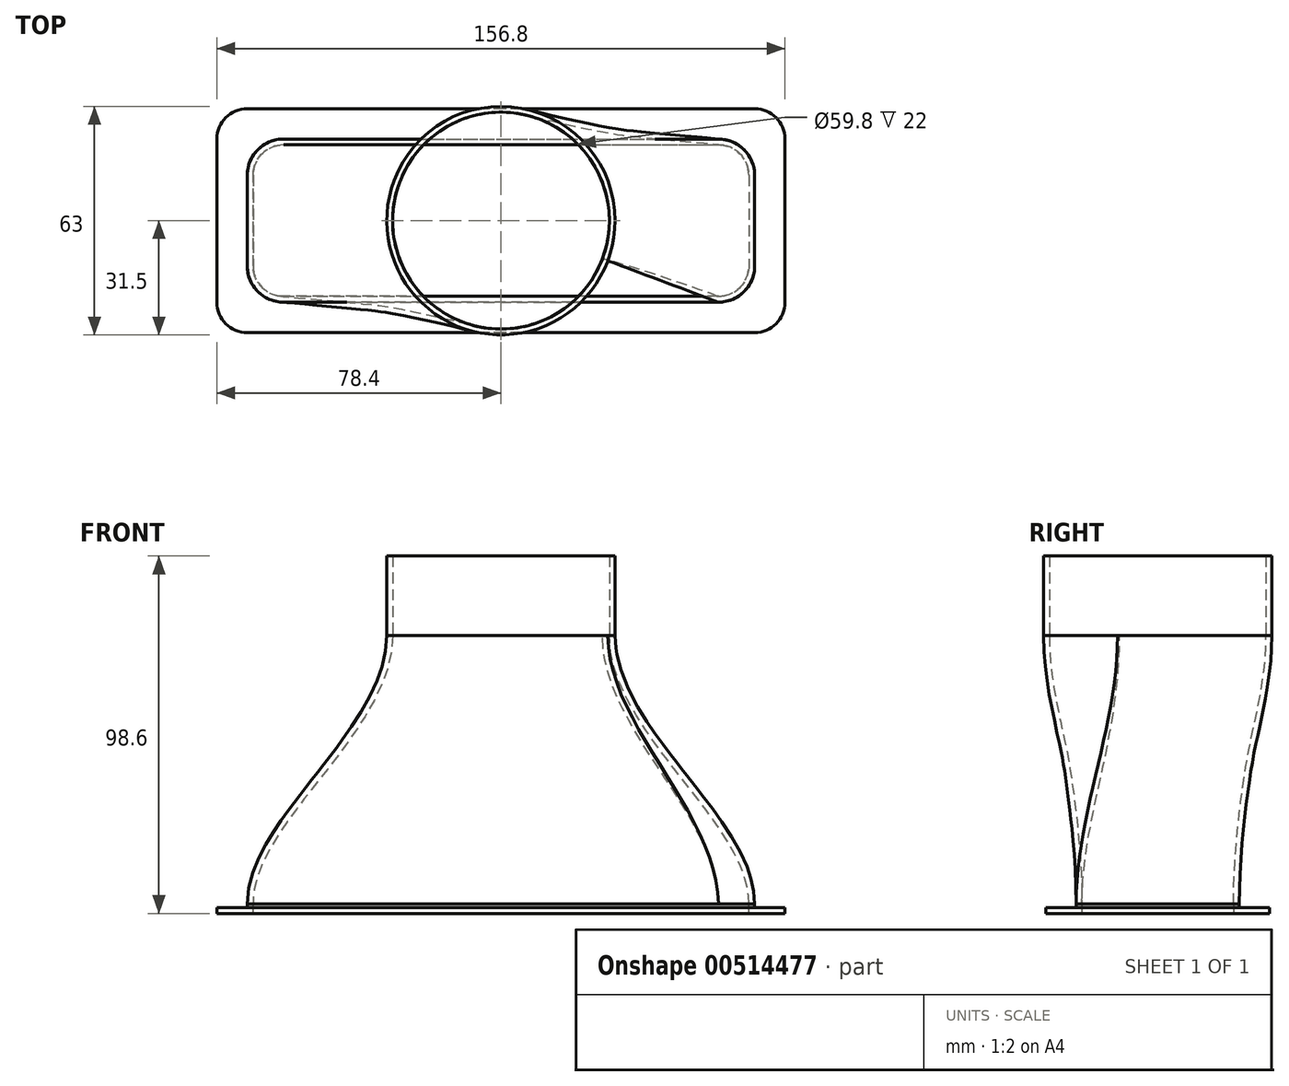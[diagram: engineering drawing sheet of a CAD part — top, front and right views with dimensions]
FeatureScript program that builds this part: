
annotation { "Feature Type Name" : "Feature", "Feature Type Description" : "" }
export const myFeature = defineFeature(function(context is Context, id is Id, definition is map)
    precondition{}
    {
        {
            var Q0;
            Q0=qCreatedBy(makeId("Top.planeOp"),FACE);
            var sketch = newSketch(context, id + "F0", { "sketchPlane" : qUnion([Q0])});
            skCircle(sketch, "E0", {"center": v(0, 0) * mm, "radius": 31.5 * mm});
            skSolve(sketch);
        }
        {
            var Q0;
            Q0 = qSketchRegion(id + "F0", true);
            extrude(context, id + "F1", {"entities" : qUnion([Q0]), "depth" : 100 * mm});
        }
        {
            var Q0;
            Q0=qCreatedBy(makeId("Top.planeOp"),FACE);
            var sketch = newSketch(context, id + "F2", { "sketchPlane" : qUnion([Q0])});
            skLineSegment(sketch, "E1.bottom", {"start": v(60, -22.5) * mm, "end": v(-60, -22.5) * mm});
            skLineSegment(sketch, "E1.top", {"start": v(60, 22.5) * mm, "end": v(-60, 22.5) * mm});
            skLineSegment(sketch, "E1.left", {"start": v(70, -12.5) * mm, "end": v(70, 12.5) * mm});
            skLineSegment(sketch, "E1.right", {"start": v(-70, -12.5) * mm, "end": v(-70, 12.5) * mm});
            skPoint(sketch, "E1.middle", {"position": v(0, 0) * mm});
            skPoint(sketch, "E2.visualSharp", {"position": v(-70, 22.5) * mm});
            skArc(sketch, "E2.filletArc", {"start": v(-60, 22.5) * mm, "mid": v(-67.07, 19.57) * mm, "end": v(-70, 12.5) * mm});
            skPoint(sketch, "E3.visualSharp", {"position": v(-70, -22.5) * mm});
            skArc(sketch, "E3.filletArc", {"start": v(-70, -12.5) * mm, "mid": v(-67.07, -19.57) * mm, "end": v(-60, -22.5) * mm});
            skPoint(sketch, "E4.visualSharp", {"position": v(70, 22.5) * mm});
            skArc(sketch, "E4.filletArc", {"start": v(70, 12.5) * mm, "mid": v(67.07, 19.57) * mm, "end": v(60, 22.5) * mm});
            skPoint(sketch, "E5.visualSharp", {"position": v(70, -22.5) * mm});
            skArc(sketch, "E5.filletArc", {"start": v(60, -22.5) * mm, "mid": v(67.07, -19.57) * mm, "end": v(70, -12.5) * mm});
            skSolve(sketch);
        }
        {
            var Q0;
            Q0=makeQuery(id+"F486plCCYYAXnXF_1.boolean.opBoolean","MERGE",FACE,{"derivedFrom":[makeQuery(id+"F1.opExtrude","CAP_FACE",FACE,{"disambiguationData":[OSD([sQuery(id+"F0.wireOp",EDGE,"E0")])],"isStart":true}),makeQuery(id+"F486plCCYYAXnXF_1.opExtrude","CAP_FACE",FACE,{"disambiguationData":[OSD([sQuery(id+"F2.wireOp",EDGE,"E1.bottom"),sQuery(id+"F2.wireOp",EDGE,"E1.top"),sQuery(id+"F2.wireOp",EDGE,"E1.left"),sQuery(id+"F2.wireOp",EDGE,"E1.right"),sQuery(id+"F2.wireOp",EDGE,"E2.filletArc"),sQuery(id+"F2.wireOp",EDGE,"E3.filletArc"),sQuery(id+"F2.wireOp",EDGE,"E4.filletArc"),sQuery(id+"F2.wireOp",EDGE,"E5.filletArc")])],"isStart":true})]});
            var sketch = newSketch(context, id + "F3", { "sketchPlane" : qUnion([Q0])});
            skCircle(sketch, "E6", {"center": v(0, 0) * mm, "radius": 31.5 * mm});
            skSolve(sketch);
        }
        {
            var Q0;
            Q0 = qSketchRegion(id + "F3", true);
            extrude(context, id + "F4", {"entities" : qUnion([Q0]), "operationType" : NewBodyOperationType.REMOVE, "oppositeDirection" : true, "depth" : 98 * mm});
        }
        {
            var Q0;
            Q0=makeQuery(id+"F2.imprint","IMPRINT",FACE,{"disambiguationData":[TD([[makeQuery(id+"F2.imprint","IMPRINT",EDGE,{"derivedFrom":sQuery(id+"F2.wireOp",EDGE,"E1.bottom")}),-1.0]])]});
            extrude(context, id + "F5", {"entities" : qUnion([Q0]), "depth" : 4 * mm});
        }
        {
            var Q0;
            Q0=makeQuery(id+"F4.boolean.opBoolean","COPY",FACE,{"derivedFrom":makeQuery(id+"F4.opExtrude","CAP_FACE",FACE,{"disambiguationData":[OSD([sQuery(id+"F3.wireOp",EDGE,"E6")])],"isStart":false})});
            extrude(context, id + "F6", {"entities" : qUnion([Q0]), "operationType" : NewBodyOperationType.ADD, "depth" : 20 * mm});
        }
        {
            var Q1;
            Q1=makeQuery(id+"F5.opExtrude","CAP_FACE",FACE,{"disambiguationData":[OSD([sQuery(id+"F2.wireOp",EDGE,"E1.bottom"),sQuery(id+"F2.wireOp",EDGE,"E1.top"),sQuery(id+"F2.wireOp",EDGE,"E1.left"),sQuery(id+"F2.wireOp",EDGE,"E1.right"),sQuery(id+"F2.wireOp",EDGE,"E2.filletArc"),sQuery(id+"F2.wireOp",EDGE,"E3.filletArc"),sQuery(id+"F2.wireOp",EDGE,"E4.filletArc"),sQuery(id+"F2.wireOp",EDGE,"E5.filletArc")])],"isStart":false});
            var Q2;
            Q2=makeQuery(id+"F6.opExtrude","CAP_FACE",FACE,{"disambiguationData":[OSD([sQuery(id+"F3.wireOp",EDGE,"E6")])],"isStart":false});
            loft(context, id + "F7", {"operationType" : NewBodyOperationType.ADD, "startCondition" : LoftEndDerivativeType.NORMAL_TO_PROFILE, "startMagnitude" : 1, "endCondition" : LoftEndDerivativeType.NORMAL_TO_PROFILE, "endMagnitude" : 1, "sheetProfilesArray" : [{ "sheetProfileEntities" : qUnion([Q1]) }, { "sheetProfileEntities" : qUnion([Q2]) }]});
        }
        {
            var Q0;
            Q0=makeQuery(id+"F5.opExtrude","CAP_FACE",FACE,{"disambiguationData":[OSD([sQuery(id+"F2.wireOp",EDGE,"E1.bottom"),sQuery(id+"F2.wireOp",EDGE,"E1.top"),sQuery(id+"F2.wireOp",EDGE,"E1.left"),sQuery(id+"F2.wireOp",EDGE,"E1.right"),sQuery(id+"F2.wireOp",EDGE,"E2.filletArc"),sQuery(id+"F2.wireOp",EDGE,"E3.filletArc"),sQuery(id+"F2.wireOp",EDGE,"E4.filletArc"),sQuery(id+"F2.wireOp",EDGE,"E5.filletArc")])],"isStart":true});
            var sketch = newSketch(context, id + "F8", { "sketchPlane" : qUnion([Q0])});
            skLineSegment(sketch, "E7.bottom", {"start": v(80, -32.5) * mm, "end": v(-80, -32.5) * mm});
            skLineSegment(sketch, "E7.top", {"start": v(80, 32.5) * mm, "end": v(-80, 32.5) * mm});
            skLineSegment(sketch, "E7.left", {"start": v(80, -32.5) * mm, "end": v(80, 32.5) * mm});
            skLineSegment(sketch, "E7.right", {"start": v(-80, -32.5) * mm, "end": v(-80, 32.5) * mm});
            skPoint(sketch, "E7.middle", {"position": v(0, 0) * mm});
            skSolve(sketch);
        }
        {
            var Q0;
            Q0 = qSketchRegion(id + "F8", true);
            extrude(context, id + "F9", {"entities" : qUnion([Q0]), "operationType" : NewBodyOperationType.ADD, "oppositeDirection" : true, "depth" : 3 * mm});
        }
        {
            var Q0;
            Q0=makeQuery(id+"F9.opExtrude","SWEPT_EDGE",EDGE,{"disambiguationData":[OSD([sQuery(id+"F8.wireOp",EDGE,"E7.top"),sQuery(id+"F8.wireOp",EDGE,"E7.left")])]});
            var Q1;
            Q1=makeQuery(id+"F9.opExtrude","SWEPT_EDGE",EDGE,{"disambiguationData":[OSD([sQuery(id+"F8.wireOp",EDGE,"E7.bottom"),sQuery(id+"F8.wireOp",EDGE,"E7.left")])]});
            var Q2;
            Q2=makeQuery(id+"F9.opExtrude","SWEPT_EDGE",EDGE,{"disambiguationData":[OSD([sQuery(id+"F8.wireOp",EDGE,"E7.top"),sQuery(id+"F8.wireOp",EDGE,"E7.right")])]});
            var Q3;
            Q3=makeQuery(id+"F9.opExtrude","SWEPT_EDGE",EDGE,{"disambiguationData":[OSD([sQuery(id+"F8.wireOp",EDGE,"E7.bottom"),sQuery(id+"F8.wireOp",EDGE,"E7.right")])]});
            fillet(context, id + "F10", {"entities" : qUnion([Q0, Q1, Q2, Q3]), "radius" : 10 * mm, "tangentPropagation" : true, "allowEdgeOverflow" : false});
        }
        {
            var Q0;
            Q0=makeQuery(id+"F1.opExtrude","CAP_FACE",FACE,{"disambiguationData":[OSD([sQuery(id+"F0.wireOp",EDGE,"E0")])],"isStart":false});
            var Q1;
            Q1=makeQuery(id+"F9.boolean.opBoolean","MERGE",FACE,{"derivedFrom":[makeQuery(id+"F5.opExtrude","CAP_FACE",FACE,{"disambiguationData":[OSD([sQuery(id+"F2.wireOp",EDGE,"E1.bottom"),sQuery(id+"F2.wireOp",EDGE,"E1.top"),sQuery(id+"F2.wireOp",EDGE,"E1.left"),sQuery(id+"F2.wireOp",EDGE,"E1.right"),sQuery(id+"F2.wireOp",EDGE,"E2.filletArc"),sQuery(id+"F2.wireOp",EDGE,"E3.filletArc"),sQuery(id+"F2.wireOp",EDGE,"E4.filletArc"),sQuery(id+"F2.wireOp",EDGE,"E5.filletArc")])],"isStart":true}),makeQuery(id+"F9.opExtrude","CAP_FACE",FACE,{"disambiguationData":[OSD([sQuery(id+"F8.wireOp",EDGE,"E7.bottom"),sQuery(id+"F8.wireOp",EDGE,"E7.top"),sQuery(id+"F8.wireOp",EDGE,"E7.left"),sQuery(id+"F8.wireOp",EDGE,"E7.right")])],"isStart":true})]});
            shell(context, id + "F11", {"entities" : qUnion([Q0, Q1]), "thickness" : 1.6 * mm});
        }
        {
            var Q0;
            Q0=makeQuery(id+"F9.boolean.opBoolean","MERGE",FACE,{"derivedFrom":[makeQuery(id+"F5.opExtrude","CAP_FACE",FACE,{"disambiguationData":[OSD([sQuery(id+"F2.wireOp",EDGE,"E1.bottom"),sQuery(id+"F2.wireOp",EDGE,"E1.top"),sQuery(id+"F2.wireOp",EDGE,"E1.left"),sQuery(id+"F2.wireOp",EDGE,"E1.right"),sQuery(id+"F2.wireOp",EDGE,"E2.filletArc"),sQuery(id+"F2.wireOp",EDGE,"E3.filletArc"),sQuery(id+"F2.wireOp",EDGE,"E4.filletArc"),sQuery(id+"F2.wireOp",EDGE,"E5.filletArc")])],"isStart":true}),makeQuery(id+"F9.opExtrude","CAP_FACE",FACE,{"disambiguationData":[OSD([sQuery(id+"F8.wireOp",EDGE,"E7.bottom"),sQuery(id+"F8.wireOp",EDGE,"E7.top"),sQuery(id+"F8.wireOp",EDGE,"E7.left"),sQuery(id+"F8.wireOp",EDGE,"E7.right")])],"isStart":true})]});
            extrude(context, id + "F12", {"entities" : qUnion([Q0]), "operationType" : NewBodyOperationType.REMOVE, "oppositeDirection" : true, "depth" : 25 * mm});
        }
    });
